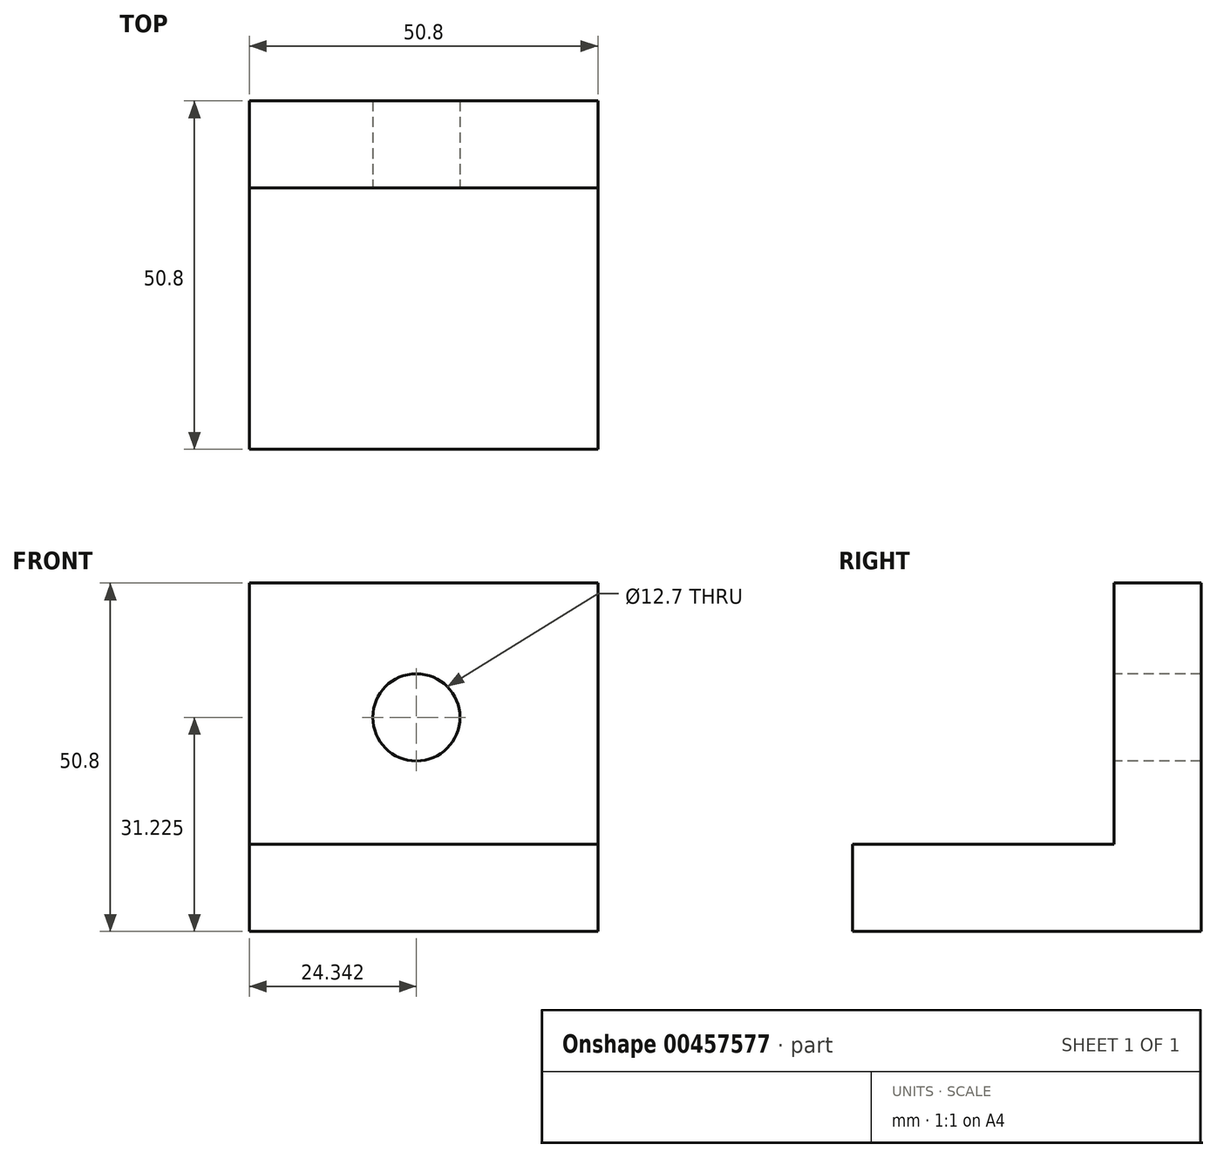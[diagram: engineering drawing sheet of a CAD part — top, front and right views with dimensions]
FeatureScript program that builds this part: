
annotation { "Feature Type Name" : "Feature", "Feature Type Description" : "" }
export const myFeature = defineFeature(function(context is Context, id is Id, definition is map)
    precondition{}
    {
        {
            var Q0;
            Q0=qCreatedBy(makeId("Top.planeOp"),FACE);
            var sketch = newSketch(context, id + "F0", { "sketchPlane" : qUnion([Q0])});
            skLineSegment(sketch, "E0.bottom", {"start": v(0, 0) * mm, "end": v(50.8, 0) * mm});
            skLineSegment(sketch, "E0.top", {"start": v(0, -50.8) * mm, "end": v(50.8, -50.8) * mm});
            skLineSegment(sketch, "E0.left", {"start": v(0, 0) * mm, "end": v(0, -50.8) * mm});
            skLineSegment(sketch, "E0.right", {"start": v(50.8, 0) * mm, "end": v(50.8, -50.8) * mm});
            skSolve(sketch);
        }
        {
            var Q0;
            Q0=makeQuery(id+"F0.imprint","IMPRINT",FACE,{"disambiguationData":[TD([[makeQuery(id+"F0.imprint","IMPRINT",EDGE,{"derivedFrom":sQuery(id+"F0.wireOp",EDGE,"E0.bottom")}),-1.0]])]});
            extrude(context, id + "F1", {"entities" : qUnion([Q0]), "depth" : 12.7 * mm});
        }
        {
            var Q0;
            Q0=qCreatedBy(makeId("Top.planeOp"),FACE);
            var sketch = newSketch(context, id + "F2", { "sketchPlane" : qUnion([Q0])});
            skLineSegment(sketch, "E1.bottom", {"start": v(0, 0) * mm, "end": v(50.8, 0) * mm});
            skLineSegment(sketch, "E1.top", {"start": v(0, -12.7) * mm, "end": v(50.8, -12.7) * mm});
            skLineSegment(sketch, "E1.left", {"start": v(0, 0) * mm, "end": v(0, -12.7) * mm});
            skLineSegment(sketch, "E1.right", {"start": v(50.8, 0) * mm, "end": v(50.8, -12.7) * mm});
            skSolve(sketch);
        }
        {
            var Q0;
            Q0 = qSketchRegion(id + "F2", true);
            extrude(context, id + "F3", {"entities" : qUnion([Q0]), "operationType" : NewBodyOperationType.ADD, "depth" : 50.8 * mm});
        }
        {
            var Q0;
            Q0=qCreatedBy(makeId("Front.planeOp"),FACE);
            var sketch = newSketch(context, id + "F4", { "sketchPlane" : qUnion([Q0])});
            skLineSegment(sketch, "E2", {"start": v(0, 49.55) * mm, "end": v(48.68, 49.55) * mm, "construction": true});
            skLineSegment(sketch, "E3", {"start": v(48.68, 49.55) * mm, "end": v(48.68, 0) * mm, "construction": true});
            skLineSegment(sketch, "E4", {"start": v(48.68, 0) * mm, "end": v(0, 0) * mm, "construction": true});
            skLineSegment(sketch, "E5", {"start": v(0, 0) * mm, "end": v(0, 49.55) * mm, "construction": true});
            skCircle(sketch, "E6", {"center": v(24.34, 24.77) * mm, "radius": 6.45 * mm, "construction": true});
            skPoint(sketch, "E6.centerSnap0", {"position": v(0, 24.77) * mm});
            skPoint(sketch, "E6.centerSnap1", {"position": v(24.34, 49.55) * mm});
            skCircle(sketch, "E7", {"center": v(24.34, 31.22) * mm, "radius": 6.35 * mm});
            skSolve(sketch);
        }
        {
            var Q0;
            Q0 = qSketchRegion(id + "F4", true);
            extrude(context, id + "F5", {"entities" : qUnion([Q0]), "operationType" : NewBodyOperationType.REMOVE, "endBound" : BoundingType.SYMMETRIC, "oppositeDirection" : true, "depth" : 25.4 * mm});
        }
    });
